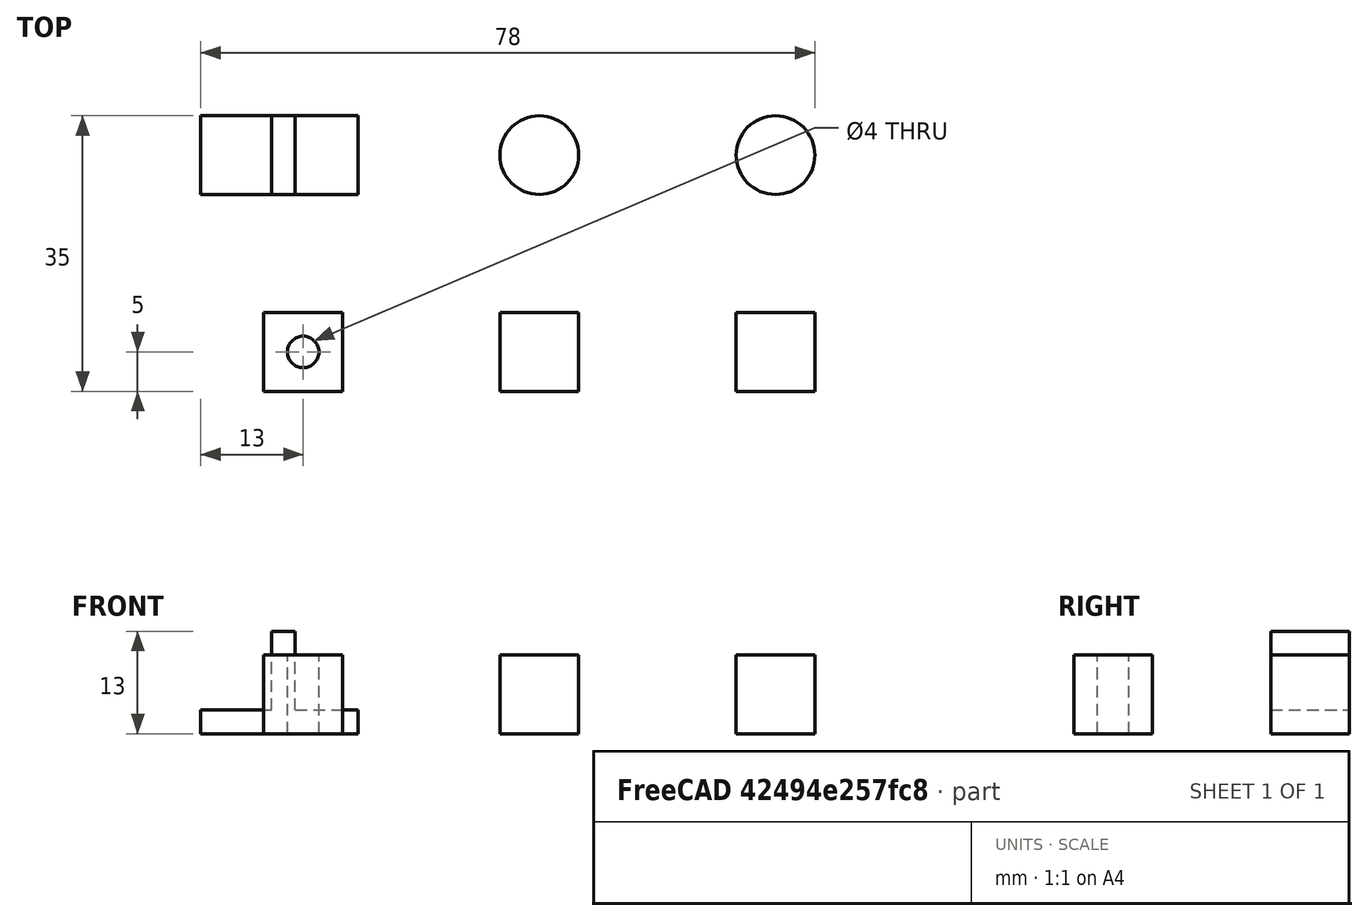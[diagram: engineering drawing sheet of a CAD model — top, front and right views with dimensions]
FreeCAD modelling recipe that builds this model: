
FCSTD DOCUMENT
Label: tutorial-ini
objects: Part::Box×5, Part::Cylinder×3, Part::Cut×1, Part::MultiFuse×1
note: 10 computed .brp shape members not serialized (recipe doc carries the construction recipe); baked Part::Feature solids carry a one-line shape summary decoded from their .brp

FEATURE [Part::Box] Box  label="Cubo-1"
  Height = 10
  Length = 10
  Placement = pos=(60,0,0) rot=(0,0,1;0rad)
  Width = 10
FEATURE [Part::Box] Box001
  Height = 10
  Length = 10
  Width = 10
FEATURE [Part::Box] Box002  label="Cubo-2"
  Height = 10
  Length = 10
  Placement = pos=(30,0,0) rot=(0,0,1;0rad)
  Width = 10
FEATURE [Part::Cylinder] Cylinder
  Angle = 360
  Height = 20
  Placement = pos=(5,5,-2) rot=(0,0,1;0rad)
  Radius = 2
FEATURE [Part::Cut] Cut  label="Cubo-3"
  Base = -> Box001
  Tool = -> Cylinder
FEATURE [Part::Cylinder] Cylinder001  label="Cilindro-1"
  Angle = 360
  Height = 10
  Placement = pos=(65,30,0) rot=(0,0,1;0rad)
  Radius = 5
FEATURE [Part::Cylinder] Cylinder002  label="Cilindro-2"
  Angle = 360
  Height = 10
  Placement = pos=(35,30,0) rot=(0,0,1;0rad)
  Radius = 5
FEATURE [Part::Box] Box003
  Height = 3
  Length = 20
  Placement = pos=(-8,25,0) rot=(0,0,1;0rad)
  Width = 10
FEATURE [Part::Box] Box004
  Height = 10
  Length = 3
  Placement = pos=(1,25,3) rot=(0,0,1;0rad)
  Width = 10
FEATURE [Part::MultiFuse] Fusion  label="union-90"
  Shapes = -> [Box003,Box004]
